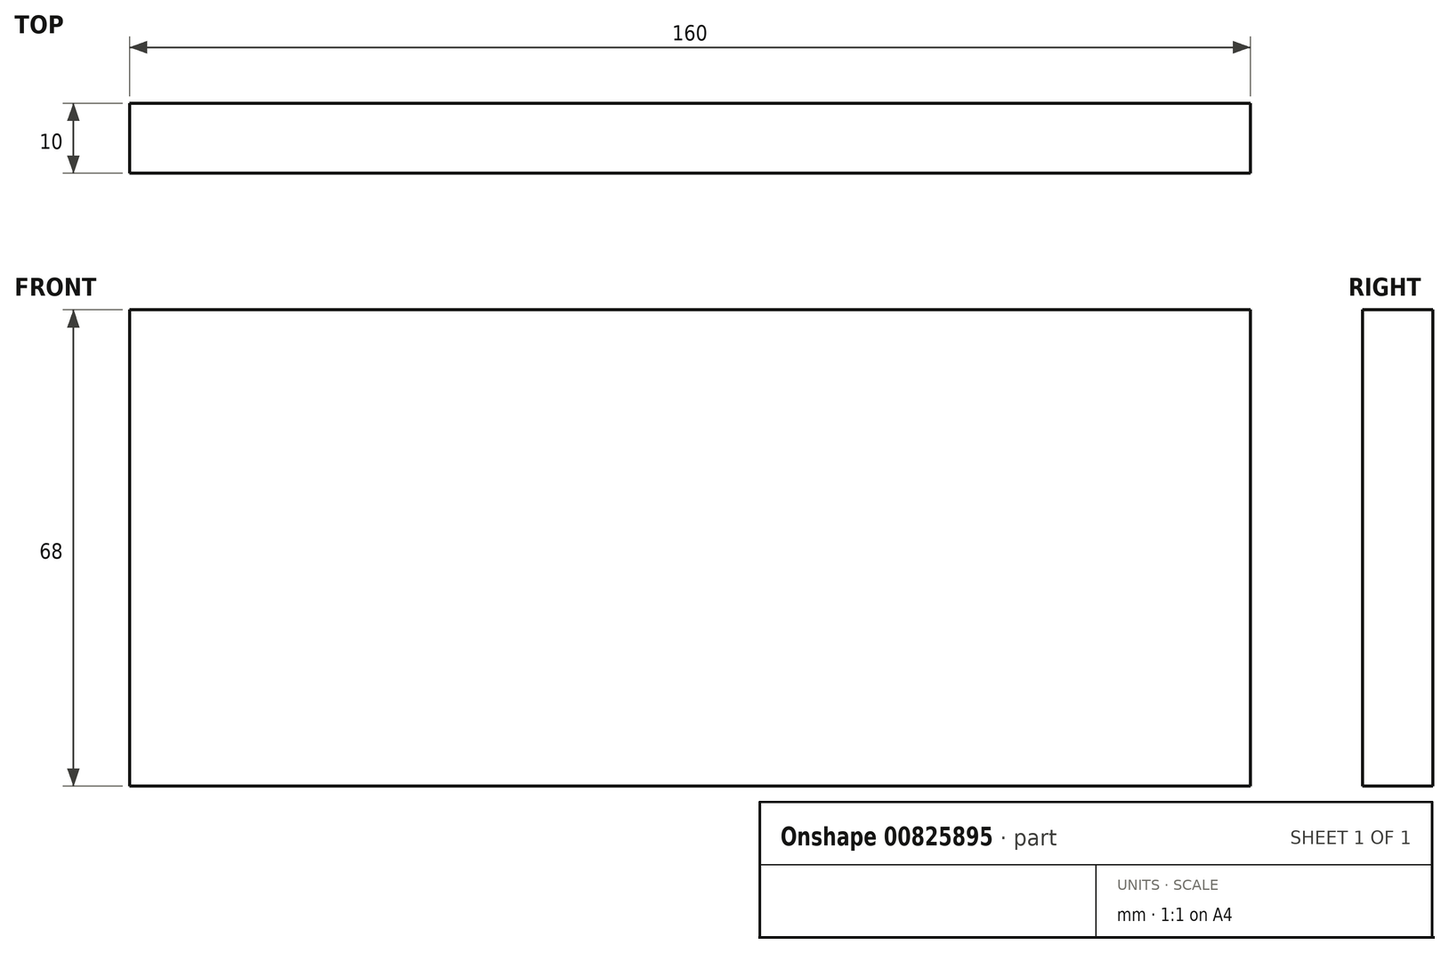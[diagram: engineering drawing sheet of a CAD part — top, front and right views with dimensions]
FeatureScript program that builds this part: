
annotation { "Feature Type Name" : "Feature", "Feature Type Description" : "" }
export const myFeature = defineFeature(function(context is Context, id is Id, definition is map)
    precondition{}
    {
        {
            var Q0;
            Q0=qCreatedBy(makeId("Right.planeOp"),FACE);
            var sketch = newSketch(context, id + "F0", { "sketchPlane" : qUnion([Q0])});
            skLineSegment(sketch, "E0", {"start": v(18.85, 47.2) * mm, "end": v(18.85, -20.8) * mm});
            skLineSegment(sketch, "E1", {"start": v(18.85, 47.2) * mm, "end": v(28.85, 47.2) * mm});
            skLineSegment(sketch, "E2", {"start": v(28.85, 47.2) * mm, "end": v(28.85, -20.8) * mm});
            skLineSegment(sketch, "E3", {"start": v(18.85, -20.8) * mm, "end": v(28.85, -20.8) * mm});
            skSolve(sketch);
        }
        {
            var Q0;
            Q0 = qSketchRegion(id + "F0", true);
            extrude(context, id + "F1", {"entities" : qUnion([Q0]), "depth" : 160 * mm, "offsetDistance" : 25 * mm});
        }
    });
